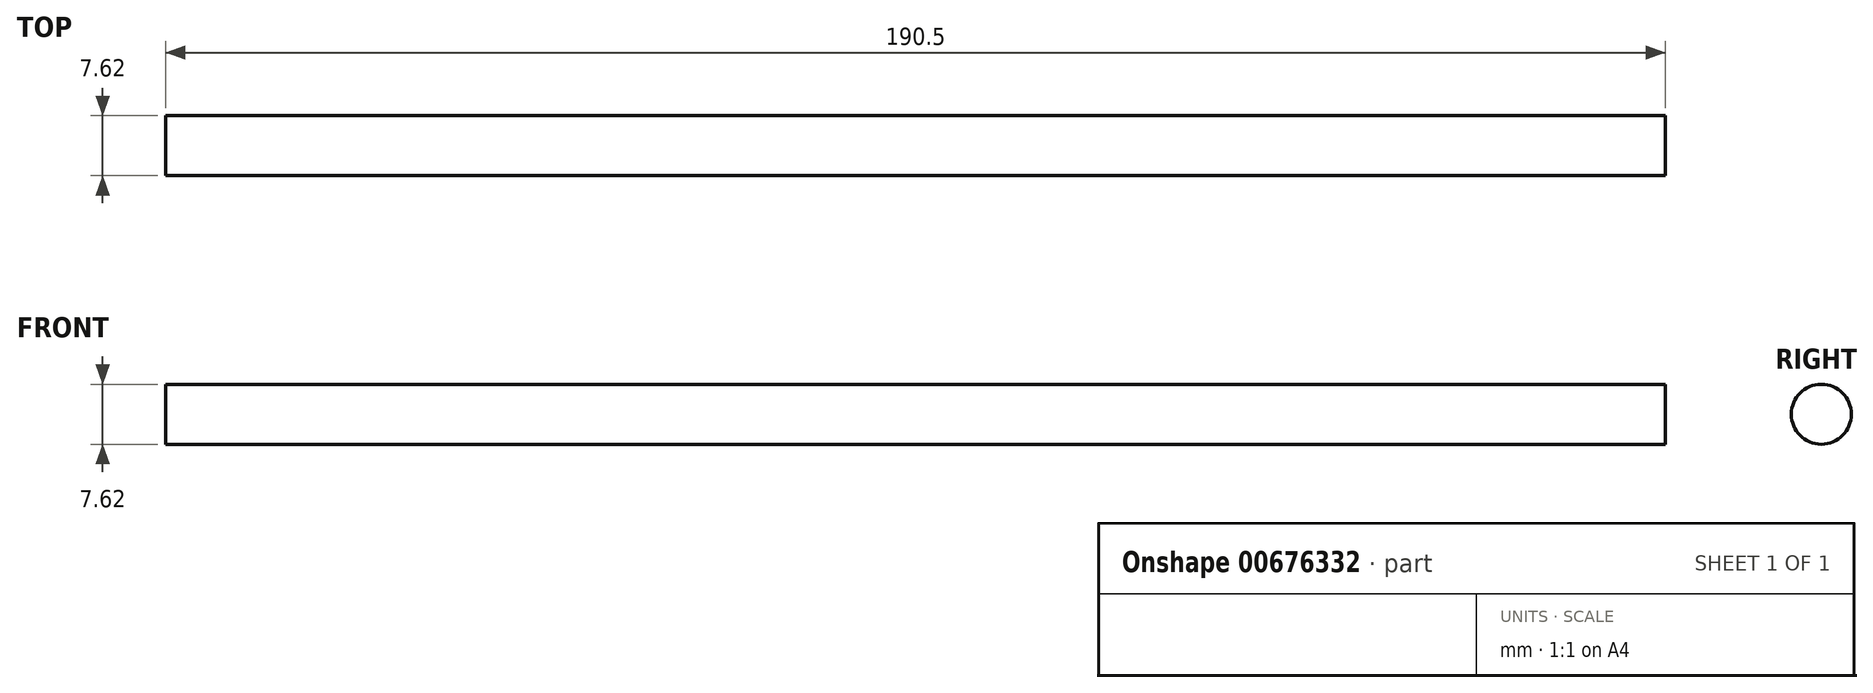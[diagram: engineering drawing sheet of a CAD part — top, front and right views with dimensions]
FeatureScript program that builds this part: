
annotation { "Feature Type Name" : "Feature", "Feature Type Description" : "" }
export const myFeature = defineFeature(function(context is Context, id is Id, definition is map)
    precondition{}
    {
        {
            var Q0;
            Q0=qCreatedBy(makeId("Right.planeOp"),FACE);
            var sketch = newSketch(context, id + "F0", { "sketchPlane" : qUnion([Q0])});
            skCircle(sketch, "E0", {"center": v(0, 0) * mm, "radius": 3.81 * mm});
            skSolve(sketch);
        }
        {
            var Q0;
            Q0 = qSketchRegion(id + "F0", true);
            extrude(context, id + "F1", {"entities" : qUnion([Q0]), "depth" : 190.5 * mm, "offsetDistance" : 25.4 * mm});
        }
    });
